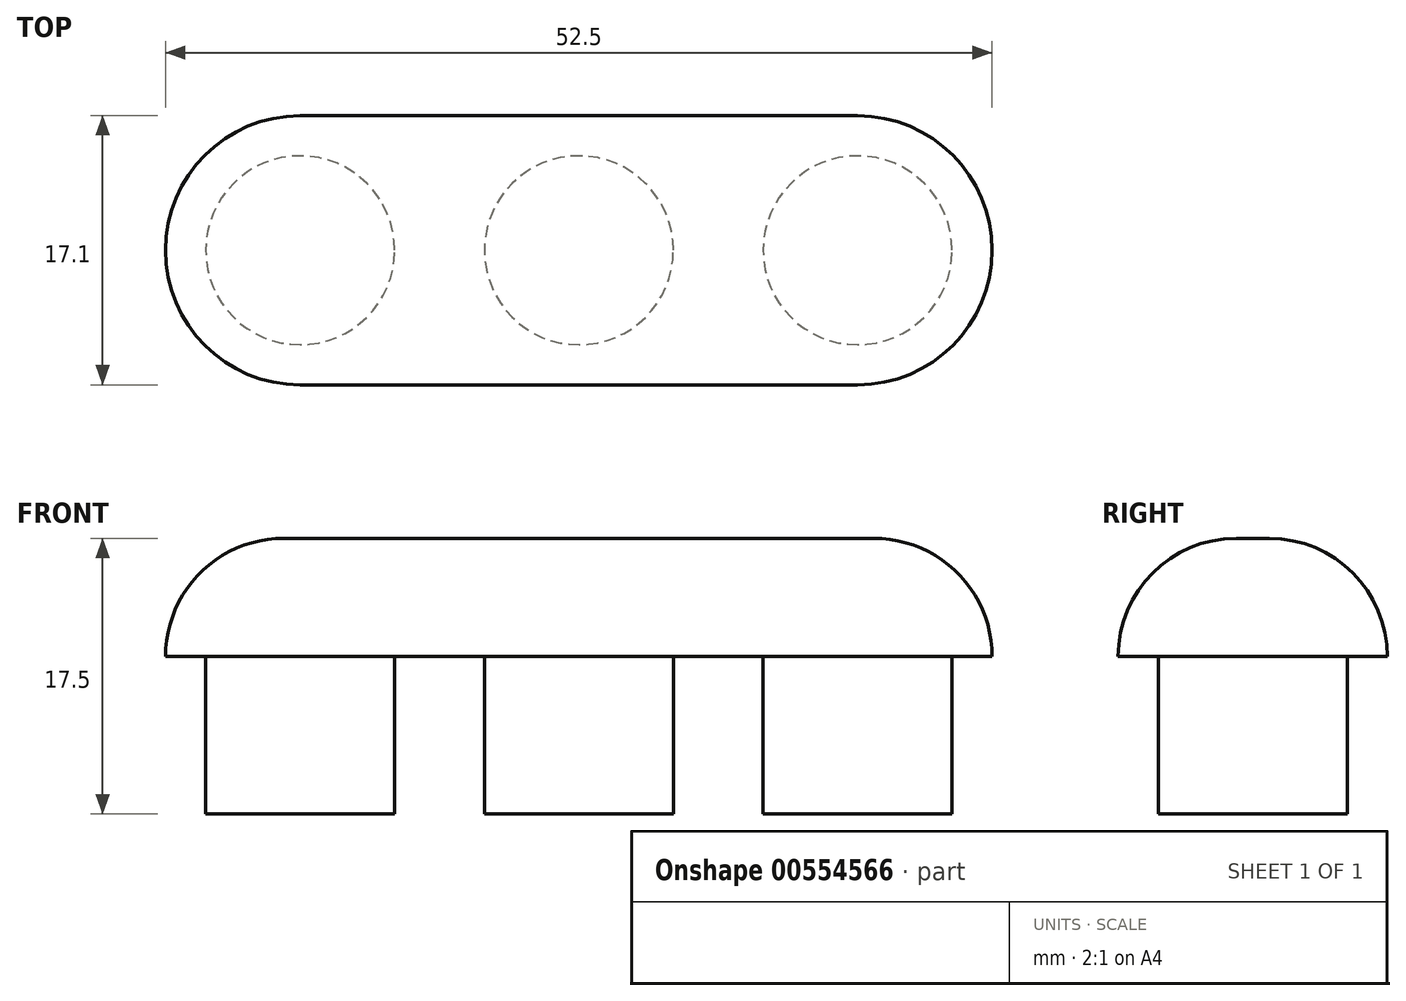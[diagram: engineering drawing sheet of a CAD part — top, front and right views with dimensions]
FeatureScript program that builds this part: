
annotation { "Feature Type Name" : "Feature", "Feature Type Description" : "" }
export const myFeature = defineFeature(function(context is Context, id is Id, definition is map)
    precondition{}
    {
        {
            var Q0;
            Q0=qCreatedBy(makeId("Top.planeOp"),FACE);
            var sketch = newSketch(context, id + "F0", { "sketchPlane" : qUnion([Q0])});
            skLineSegment(sketch, "E0.bottom", {"start": v(-53.21, 40.4) * mm, "end": v(-17.81, 40.4) * mm});
            skLineSegment(sketch, "E0.top", {"start": v(-53.21, 23.3) * mm, "end": v(-17.81, 23.3) * mm});
            skLineSegment(sketch, "E0.left", {"start": v(-61.76, 31.85) * mm, "end": v(-61.76, 31.85) * mm});
            skLineSegment(sketch, "E0.right", {"start": v(-9.26, 31.85) * mm, "end": v(-9.26, 31.85) * mm});
            skPoint(sketch, "E1.visualSharp", {"position": v(-61.76, 40.4) * mm});
            skArc(sketch, "E1.filletArc", {"start": v(-53.21, 40.4) * mm, "mid": v(-59.26, 37.9) * mm, "end": v(-61.76, 31.85) * mm});
            skPoint(sketch, "E2.visualSharp", {"position": v(-61.76, 23.3) * mm});
            skArc(sketch, "E2.filletArc", {"start": v(-61.76, 31.85) * mm, "mid": v(-59.26, 25.8) * mm, "end": v(-53.21, 23.3) * mm});
            skPoint(sketch, "E3.visualSharp", {"position": v(-9.26, 40.4) * mm});
            skArc(sketch, "E3.filletArc", {"start": v(-9.26, 31.85) * mm, "mid": v(-11.77, 37.9) * mm, "end": v(-17.81, 40.4) * mm});
            skPoint(sketch, "E4.visualSharp", {"position": v(-9.26, 23.3) * mm});
            skArc(sketch, "E4.filletArc", {"start": v(-17.81, 23.3) * mm, "mid": v(-11.77, 25.8) * mm, "end": v(-9.26, 31.85) * mm});
            skPoint(sketch, "E5", {"position": v(-35.51, 40.4) * mm});
            skPoint(sketch, "E6", {"position": v(-35.51, 23.3) * mm});
            skLineSegment(sketch, "E7", {"start": v(-35.51, 23.3) * mm, "end": v(-35.51, 40.4) * mm, "construction": true});
            skPoint(sketch, "E8", {"position": v(-35.51, 31.85) * mm});
            skCircle(sketch, "E9", {"center": v(-35.51, 31.85) * mm, "radius": 6 * mm});
            skLineSegment(sketch, "E10", {"start": v(-35.51, 31.85) * mm, "end": v(-18.01, 31.85) * mm, "construction": true});
            skCircle(sketch, "E11", {"center": v(-17.81, 31.85) * mm, "radius": 6 * mm});
            skCircle(sketch, "E12", {"center": v(-53.21, 31.85) * mm, "radius": 6 * mm});
            skSolve(sketch);
        }
        {
            var Q0;
            Q0=makeQuery(id+"F0.imprint","IMPRINT",FACE,{"disambiguationData":[TD([[makeQuery(id+"F0.imprint","IMPRINT",EDGE,{"derivedFrom":sQuery(id+"F0.wireOp",EDGE,"E0.bottom")}),-1.0]])]});
            var Q1;
            Q1=makeQuery(id+"F0.imprint","IMPRINT",FACE,{"disambiguationData":[TD([[makeQuery(id+"F0.imprint","IMPRINT",EDGE,{"derivedFrom":sQuery(id+"F0.wireOp",EDGE,"E12")}),1.0]])]});
            var Q2;
            Q2=makeQuery(id+"F0.imprint","IMPRINT",FACE,{"disambiguationData":[TD([[makeQuery(id+"F0.imprint","IMPRINT",EDGE,{"derivedFrom":sQuery(id+"F0.wireOp",EDGE,"E9")}),1.0]])]});
            var Q3;
            Q3=makeQuery(id+"F0.imprint","IMPRINT",FACE,{"disambiguationData":[TD([[makeQuery(id+"F0.imprint","IMPRINT",EDGE,{"derivedFrom":sQuery(id+"F0.wireOp",EDGE,"E11")}),1.0]])]});
            extrude(context, id + "F1", {"entities" : qUnion([Q0, Q1, Q2, Q3]), "depth" : 7.5 * mm, "offsetDistance" : 25 * mm});
        }
        {
            var Q0;
            Q0=makeQuery(id+"F0.imprint","IMPRINT",FACE,{"disambiguationData":[TD([[makeQuery(id+"F0.imprint","IMPRINT",EDGE,{"derivedFrom":sQuery(id+"F0.wireOp",EDGE,"E12")}),1.0]])]});
            var Q1;
            Q1=makeQuery(id+"F0.imprint","IMPRINT",FACE,{"disambiguationData":[TD([[makeQuery(id+"F0.imprint","IMPRINT",EDGE,{"derivedFrom":sQuery(id+"F0.wireOp",EDGE,"E9")}),1.0]])]});
            var Q2;
            Q2=makeQuery(id+"F0.imprint","IMPRINT",FACE,{"disambiguationData":[TD([[makeQuery(id+"F0.imprint","IMPRINT",EDGE,{"derivedFrom":sQuery(id+"F0.wireOp",EDGE,"E11")}),1.0]])]});
            extrude(context, id + "F2", {"entities" : qUnion([Q0, Q1, Q2]), "operationType" : NewBodyOperationType.ADD, "oppositeDirection" : true, "depth" : 10 * mm, "offsetDistance" : 25 * mm});
        }
        {
            var Q0;
            Q0=makeQuery(id+"F1.opExtrude","CAP_EDGE",EDGE,{"disambiguationData":[OSD([sQuery(id+"F0.wireOp",EDGE,"E1.filletArc"),sQuery(id+"F0.wireOp",EDGE,"E2.filletArc")])],"isStart":false});
            fillet(context, id + "F3", {"entities" : qUnion([Q0]), "radius" : 7.5 * mm, "tangentPropagation" : true, "allowEdgeOverflow" : false});
        }
    });
